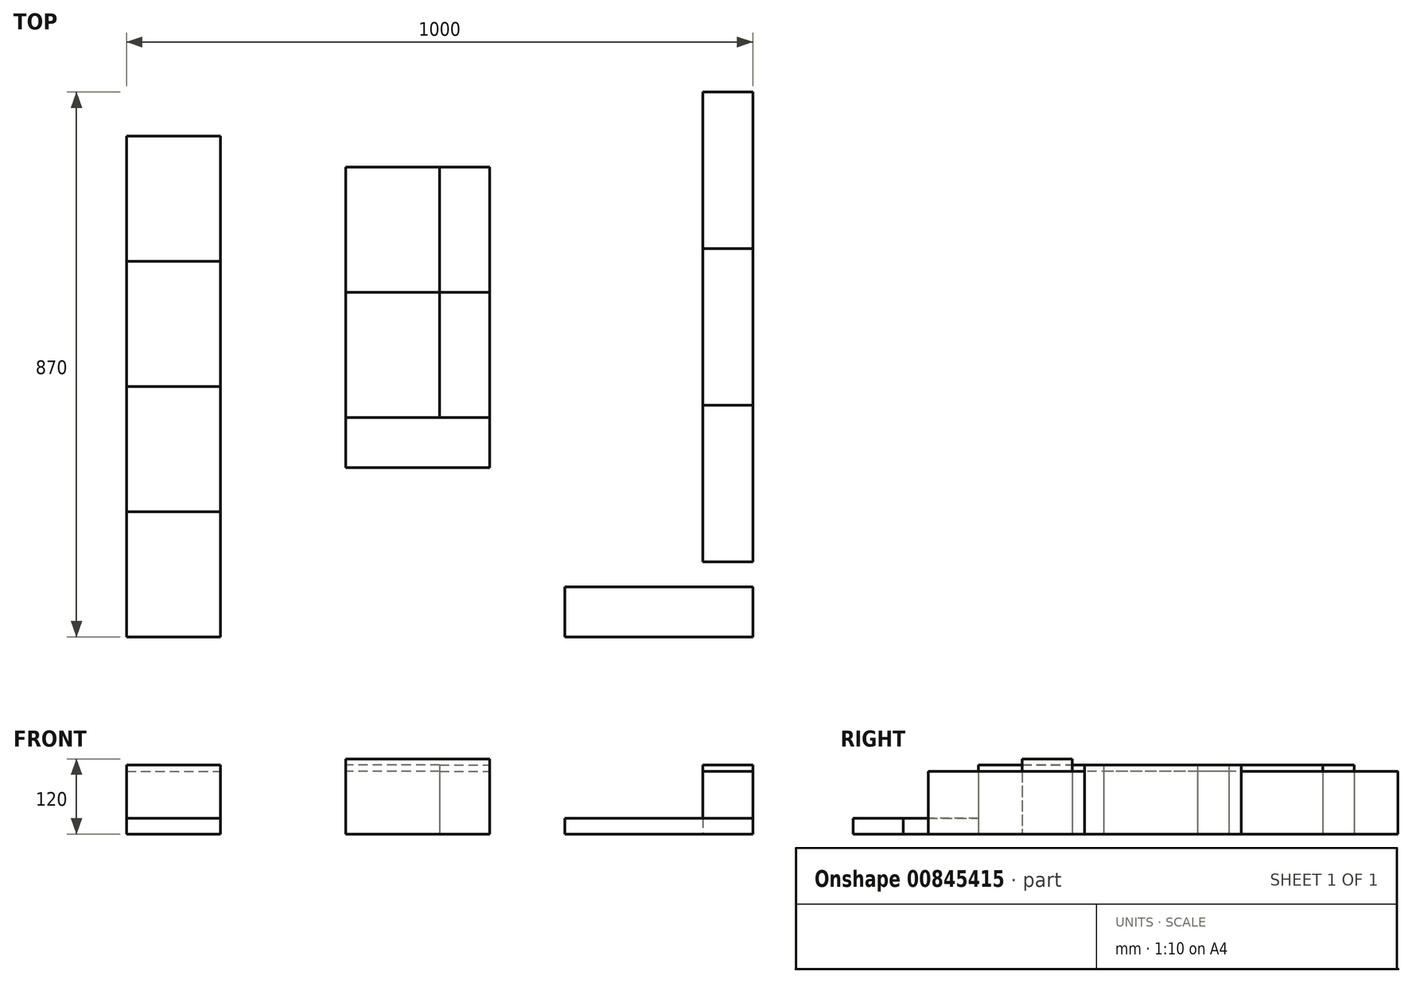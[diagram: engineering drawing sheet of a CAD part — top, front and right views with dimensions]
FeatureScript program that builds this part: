
annotation { "Feature Type Name" : "Feature", "Feature Type Description" : "" }
export const myFeature = defineFeature(function(context is Context, id is Id, definition is map)
    precondition{}
    {
        {
            var Q0;
            Q0=qCreatedBy(makeId("Top.planeOp"),FACE);
            var sketch = newSketch(context, id + "F0", { "sketchPlane" : qUnion([Q0])});
            skLineSegment(sketch, "E0.bottom", {"start": v(-500, 500) * mm, "end": v(500, 500) * mm});
            skLineSegment(sketch, "E0.top", {"start": v(-500, -500) * mm, "end": v(500, -500) * mm});
            skLineSegment(sketch, "E0.left", {"start": v(-500, 500) * mm, "end": v(-500, -500) * mm});
            skLineSegment(sketch, "E0.right", {"start": v(500, 500) * mm, "end": v(500, -500) * mm});
            skLineSegment(sketch, "E1.bottom", {"start": v(-500, 500) * mm, "end": v(-250, 500) * mm});
            skLineSegment(sketch, "E1.top", {"start": v(-500, 420) * mm, "end": v(-250, 420) * mm});
            skLineSegment(sketch, "E1.left", {"start": v(-500, 500) * mm, "end": v(-500, 420) * mm});
            skLineSegment(sketch, "E1.right", {"start": v(-250, 500) * mm, "end": v(-250, 420) * mm});
            skLineSegment(sketch, "E2.bottom", {"start": v(-250, 500) * mm, "end": v(0, 500) * mm});
            skLineSegment(sketch, "E2.top", {"start": v(-250, 420) * mm, "end": v(0, 420) * mm});
            skLineSegment(sketch, "E2.right", {"start": v(0, 500) * mm, "end": v(0, 420) * mm});
            skLineSegment(sketch, "E3.bottom", {"start": v(0, 500) * mm, "end": v(250, 500) * mm});
            skLineSegment(sketch, "E3.top", {"start": v(0, 420) * mm, "end": v(250, 420) * mm});
            skLineSegment(sketch, "E3.right", {"start": v(250, 500) * mm, "end": v(250, 420) * mm});
            skLineSegment(sketch, "E4.bottom", {"start": v(250, 500) * mm, "end": v(500, 500) * mm});
            skLineSegment(sketch, "E4.top", {"start": v(250, 420) * mm, "end": v(500, 420) * mm});
            skLineSegment(sketch, "E4.right", {"start": v(500, 500) * mm, "end": v(500, 420) * mm});
            skLineSegment(sketch, "E5.bottom", {"start": v(-500, -500) * mm, "end": v(-350, -500) * mm});
            skLineSegment(sketch, "E5.top", {"start": v(-500, -300) * mm, "end": v(-350, -300) * mm});
            skLineSegment(sketch, "E5.left", {"start": v(-500, -500) * mm, "end": v(-500, -300) * mm});
            skLineSegment(sketch, "E5.right", {"start": v(-350, -500) * mm, "end": v(-350, -300) * mm});
            skLineSegment(sketch, "E6.top", {"start": v(-500, -100) * mm, "end": v(-350, -100) * mm});
            skLineSegment(sketch, "E6.left", {"start": v(-500, -300) * mm, "end": v(-500, -100) * mm});
            skLineSegment(sketch, "E6.right", {"start": v(-350, -300) * mm, "end": v(-350, -100) * mm});
            skLineSegment(sketch, "E7.top", {"start": v(-500, 100) * mm, "end": v(-350, 100) * mm});
            skLineSegment(sketch, "E7.left", {"start": v(-500, -100) * mm, "end": v(-500, 100) * mm});
            skLineSegment(sketch, "E7.right", {"start": v(-350, -100) * mm, "end": v(-350, 100) * mm});
            skLineSegment(sketch, "E8.top", {"start": v(-500, 300) * mm, "end": v(-350, 300) * mm});
            skLineSegment(sketch, "E8.left", {"start": v(-500, 100) * mm, "end": v(-500, 300) * mm});
            skLineSegment(sketch, "E8.right", {"start": v(-350, 100) * mm, "end": v(-350, 300) * mm});
            skLineSegment(sketch, "E9.bottom", {"start": v(500, 370) * mm, "end": v(420, 370) * mm});
            skLineSegment(sketch, "E9.top", {"start": v(500, 120) * mm, "end": v(420, 120) * mm});
            skLineSegment(sketch, "E9.left", {"start": v(500, 370) * mm, "end": v(500, 120) * mm});
            skLineSegment(sketch, "E9.right", {"start": v(420, 370) * mm, "end": v(420, 120) * mm});
            skLineSegment(sketch, "E10.top", {"start": v(500, -130) * mm, "end": v(420, -130) * mm});
            skLineSegment(sketch, "E10.left", {"start": v(500, 120) * mm, "end": v(500, -130) * mm});
            skLineSegment(sketch, "E10.right", {"start": v(420, 120) * mm, "end": v(420, -130) * mm});
            skLineSegment(sketch, "E11.top", {"start": v(500, -380) * mm, "end": v(420, -380) * mm});
            skLineSegment(sketch, "E11.left", {"start": v(500, -130) * mm, "end": v(500, -380) * mm});
            skLineSegment(sketch, "E11.right", {"start": v(420, -130) * mm, "end": v(420, -380) * mm});
            skLineSegment(sketch, "E12.bottom", {"start": v(500, -500) * mm, "end": v(200, -500) * mm});
            skLineSegment(sketch, "E12.top", {"start": v(500, -420) * mm, "end": v(200, -420) * mm});
            skLineSegment(sketch, "E12.left", {"start": v(500, -500) * mm, "end": v(500, -420) * mm});
            skLineSegment(sketch, "E12.right", {"start": v(200, -500) * mm, "end": v(200, -420) * mm});
            skLineSegment(sketch, "E13.bottom", {"start": v(0, 250) * mm, "end": v(80, 250) * mm});
            skLineSegment(sketch, "E13.top", {"start": v(0, 50) * mm, "end": v(80, 50) * mm});
            skLineSegment(sketch, "E13.left", {"start": v(0, 250) * mm, "end": v(0, 50) * mm});
            skLineSegment(sketch, "E13.right", {"start": v(80, 250) * mm, "end": v(80, 50) * mm});
            skLineSegment(sketch, "E14.top", {"start": v(0, -150) * mm, "end": v(80, -150) * mm});
            skLineSegment(sketch, "E14.left", {"start": v(0, 50) * mm, "end": v(0, -150) * mm});
            skLineSegment(sketch, "E14.right", {"start": v(80, 50) * mm, "end": v(80, -150) * mm});
            skLineSegment(sketch, "E15.bottom", {"start": v(0, 50) * mm, "end": v(-150, 50) * mm});
            skLineSegment(sketch, "E15.top", {"start": v(0, 250) * mm, "end": v(-150, 250) * mm});
            skLineSegment(sketch, "E15.left", {"start": v(0, 50) * mm, "end": v(0, 250) * mm});
            skLineSegment(sketch, "E15.right", {"start": v(-150, 50) * mm, "end": v(-150, 250) * mm});
            skLineSegment(sketch, "E16.bottom", {"start": v(0, -150) * mm, "end": v(-150, -150) * mm});
            skLineSegment(sketch, "E16.left", {"start": v(0, -150) * mm, "end": v(0, 50) * mm});
            skLineSegment(sketch, "E16.right", {"start": v(-150, -150) * mm, "end": v(-150, 50) * mm});
            skLineSegment(sketch, "E17.bottom", {"start": v(-150, -150) * mm, "end": v(80, -150) * mm});
            skLineSegment(sketch, "E17.top", {"start": v(-150, -230) * mm, "end": v(80, -230) * mm});
            skLineSegment(sketch, "E17.left", {"start": v(-150, -150) * mm, "end": v(-150, -230) * mm});
            skLineSegment(sketch, "E17.right", {"start": v(80, -150) * mm, "end": v(80, -230) * mm});
            skSolve(sketch);
        }
        {
            var Q0;
            Q0=makeQuery(id+"F0.imprint","IMPRINT",FACE,{"disambiguationData":[TD([[makeQuery(id+"F0.imprint","IMPRINT",EDGE,{"derivedFrom":sQuery(id+"F0.wireOp",EDGE,"E1.bottom")}),-1.0]])]});
            var Q1;
            Q1=makeQuery(id+"F0.imprint","IMPRINT",FACE,{"disambiguationData":[TD([[makeQuery(id+"F0.imprint","IMPRINT",EDGE,{"derivedFrom":sQuery(id+"F0.wireOp",EDGE,"E3.bottom")}),-1.0]])]});
            var Q2;
            Q2=makeQuery(id+"F0.imprint","IMPRINT",FACE,{"disambiguationData":[TD([[makeQuery(id+"F0.imprint","IMPRINT",EDGE,{"derivedFrom":sQuery(id+"F0.wireOp",EDGE,"E9.bottom")}),1.0]])]});
            var Q3;
            Q3=makeQuery(id+"F0.imprint","IMPRINT",FACE,{"disambiguationData":[TD([[makeQuery(id+"F0.imprint","IMPRINT",EDGE,{"derivedFrom":sQuery(id+"F0.wireOp",EDGE,"E10.top")}),1.0]])]});
            var Q4;
            Q4=makeQuery(id+"F0.imprint","IMPRINT",FACE,{"disambiguationData":[TD([[makeQuery(id+"F0.imprint","IMPRINT",EDGE,{"derivedFrom":sQuery(id+"F0.wireOp",EDGE,"E12.bottom")}),-1.0]])]});
            var Q5;
            Q5=makeQuery(id+"F0.imprint","IMPRINT",FACE,{"disambiguationData":[TD([[makeQuery(id+"F0.imprint","IMPRINT",EDGE,{"derivedFrom":sQuery(id+"F0.wireOp",EDGE,"E5.bottom")}),1.0]])]});
            var Q6;
            Q6=makeQuery(id+"F0.imprint","IMPRINT",FACE,{"disambiguationData":[TD([[makeQuery(id+"F0.imprint","IMPRINT",EDGE,{"derivedFrom":sQuery(id+"F0.wireOp",EDGE,"E6.top")}),1.0]])]});
            var Q7;
            Q7=makeQuery(id+"F0.imprint","IMPRINT",FACE,{"disambiguationData":[TD([[makeQuery(id+"F0.imprint","IMPRINT",EDGE,{"derivedFrom":sQuery(id+"F0.wireOp",EDGE,"E15.bottom")}),1.0]])]});
            var Q8;
            Q8=makeQuery(id+"F0.imprint","IMPRINT",FACE,{"disambiguationData":[TD([[makeQuery(id+"F0.imprint","IMPRINT",EDGE,{"derivedFrom":sQuery(id+"F0.wireOp",EDGE,"E13.bottom")}),-1.0]])]});
            extrude(context, id + "F1", {"entities" : qUnion([Q0, Q1, Q2, Q3, Q4, Q5, Q6, Q7, Q8]), "depth" : 100 * mm, "offsetDistance" : 25 * mm});
        }
        {
            var Q0;
            Q0=makeQuery(id+"F0.imprint","IMPRINT",FACE,{"disambiguationData":[TD([[makeQuery(id+"F0.imprint","IMPRINT",EDGE,{"derivedFrom":sQuery(id+"F0.wireOp",EDGE,"E7.top")}),1.0]])]});
            var Q1;
            Q1=makeQuery(id+"F0.imprint","IMPRINT",FACE,{"disambiguationData":[TD([[makeQuery(id+"F0.imprint","IMPRINT",EDGE,{"derivedFrom":sQuery(id+"F0.wireOp",EDGE,"E2.bottom")}),-1.0]])]});
            var Q2;
            Q2=makeQuery(id+"F0.imprint","IMPRINT",FACE,{"disambiguationData":[TD([[makeQuery(id+"F0.imprint","IMPRINT",EDGE,{"derivedFrom":sQuery(id+"F0.wireOp",EDGE,"E4.bottom")}),-1.0]])]});
            var Q3;
            Q3=makeQuery(id+"F0.imprint","IMPRINT",FACE,{"disambiguationData":[TD([[makeQuery(id+"F0.imprint","IMPRINT",EDGE,{"derivedFrom":sQuery(id+"F0.wireOp",EDGE,"E9.top")}),1.0]])]});
            var Q4;
            Q4=makeQuery(id+"F0.imprint","IMPRINT",FACE,{"disambiguationData":[TD([[makeQuery(id+"F0.imprint","IMPRINT",EDGE,{"derivedFrom":sQuery(id+"F0.wireOp",EDGE,"E15.top")}),1.0]])]});
            var Q5;
            Q5=makeQuery(id+"F0.imprint","IMPRINT",FACE,{"disambiguationData":[TD([[makeQuery(id+"F0.imprint","IMPRINT",EDGE,{"derivedFrom":sQuery(id+"F0.wireOp",EDGE,"E13.top")}),-1.0]])]});
            var Q6;
            Q6=makeQuery(id+"F0.imprint","IMPRINT",FACE,{"disambiguationData":[TD([[makeQuery(id+"F0.imprint","IMPRINT",EDGE,{"derivedFrom":sQuery(id+"F0.wireOp",EDGE,"E5.top")}),1.0]])]});
            extrude(context, id + "F2", {"entities" : qUnion([Q0, Q1, Q2, Q3, Q4, Q5, Q6]), "depth" : 110 * mm, "offsetDistance" : 25 * mm});
        }
        {
            var Q0;
            Q0=makeQuery(id+"F0.imprint","IMPRINT",FACE,{"disambiguationData":[TD([[makeQuery(id+"F0.imprint","IMPRINT",EDGE,{"derivedFrom":sQuery(id+"F0.wireOp",EDGE,"E17.top")}),1.0]])]});
            extrude(context, id + "F3", {"entities" : qUnion([Q0]), "depth" : 120 * mm, "offsetDistance" : 25 * mm});
        }
        {
            var Q0;
            Q0=makeQuery(id+"F0.imprint","IMPRINT",FACE,{"disambiguationData":[TD([[makeQuery(id+"F0.imprint","IMPRINT",EDGE,{"derivedFrom":sQuery(id+"F0.wireOp",EDGE,"E0.top")}),1.0]])]});
            extrude(context, id + "F4", {"entities" : qUnion([Q0]), "depth" : 25 * mm, "offsetDistance" : 25 * mm});
        }
    });
